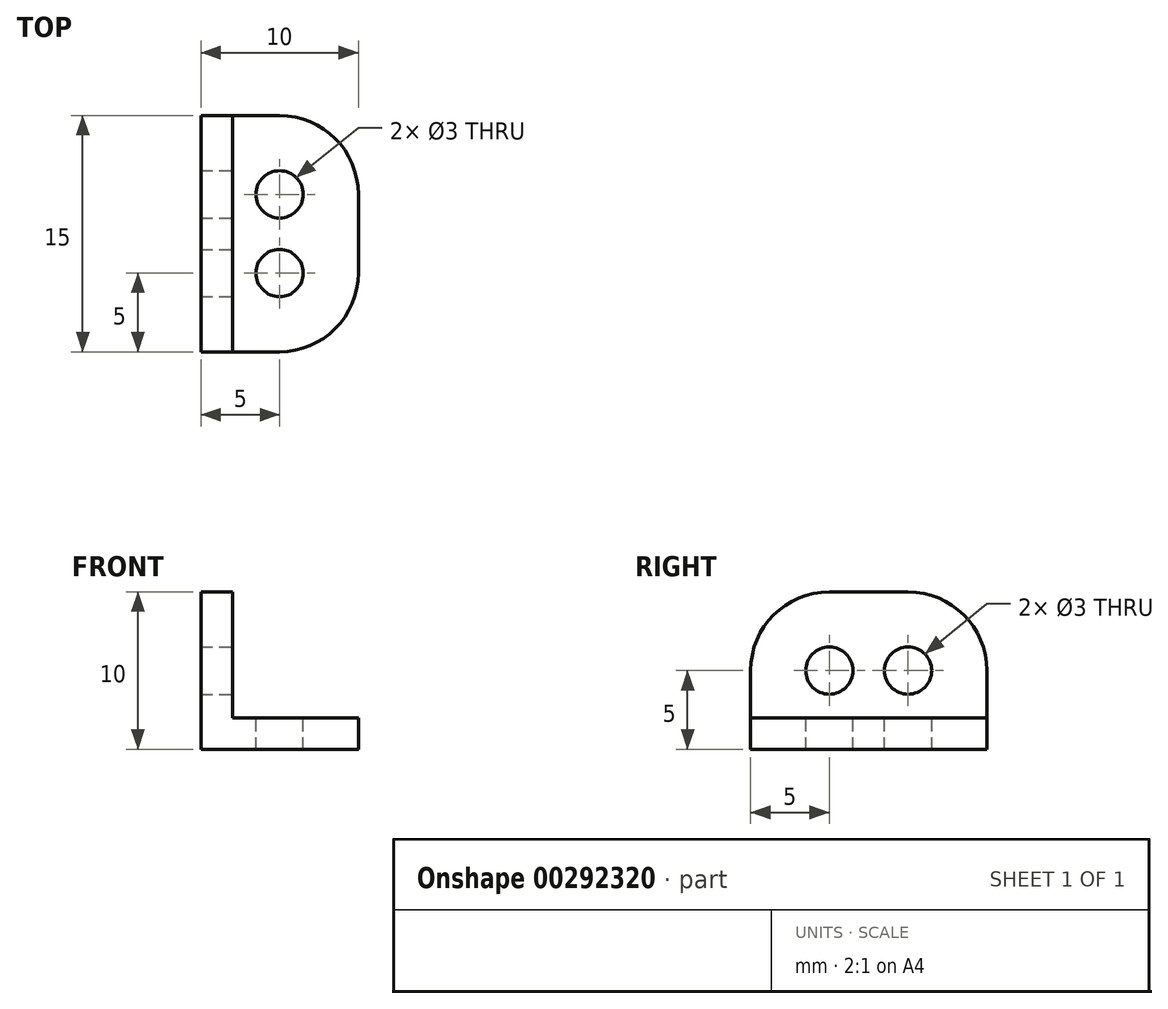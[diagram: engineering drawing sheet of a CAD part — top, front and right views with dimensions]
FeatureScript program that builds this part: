
annotation { "Feature Type Name" : "Feature", "Feature Type Description" : "" }
export const myFeature = defineFeature(function(context is Context, id is Id, definition is map)
    precondition{}
    {
        {
            var Q0;
            Q0=qCreatedBy(makeId("Front.planeOp"),FACE);
            var sketch = newSketch(context, id + "F0", { "sketchPlane" : qUnion([Q0])});
            skLineSegment(sketch, "E0", {"start": v(-5, 5) * mm, "end": v(-5, -5) * mm});
            skLineSegment(sketch, "E1", {"start": v(-5, -5) * mm, "end": v(5, -5) * mm});
            skLineSegment(sketch, "E2", {"start": v(5, -5) * mm, "end": v(5, -3) * mm});
            skLineSegment(sketch, "E3", {"start": v(5, -3) * mm, "end": v(-3, -3) * mm});
            skLineSegment(sketch, "E4", {"start": v(-3, -3) * mm, "end": v(-3, 5) * mm});
            skLineSegment(sketch, "E5", {"start": v(-3, 5) * mm, "end": v(-5, 5) * mm});
            skSolve(sketch);
        }
        {
            var Q0;
            Q0 = qSketchRegion(id + "F0", true);
            extrude(context, id + "F1", {"entities" : qUnion([Q0]), "endBound" : BoundingType.SYMMETRIC, "depth" : 15 * mm});
        }
        {
            var Q0;
            Q0=makeQuery(id+"F1.opExtrude","CAP_EDGE",EDGE,{"disambiguationData":[OSD([sQuery(id+"F0.wireOp",EDGE,"E5")])],"isStart":false});
            var Q1;
            Q1=makeQuery(id+"F1.opExtrude","CAP_EDGE",EDGE,{"disambiguationData":[OSD([sQuery(id+"F0.wireOp",EDGE,"E5")])],"isStart":true});
            var Q2;
            Q2=makeQuery(id+"F1.opExtrude","CAP_EDGE",EDGE,{"disambiguationData":[OSD([sQuery(id+"F0.wireOp",EDGE,"E2")])],"isStart":false});
            var Q3;
            Q3=makeQuery(id+"F1.opExtrude","CAP_EDGE",EDGE,{"disambiguationData":[OSD([sQuery(id+"F0.wireOp",EDGE,"E2")])],"isStart":true});
            fillet(context, id + "F2", {"entities" : qUnion([Q0, Q1, Q2, Q3]), "radius" : 5 * mm, "tangentPropagation" : true, "allowEdgeOverflow" : false});
        }
        {
            var Q0;
            Q0=qCreatedBy(makeId("Right.planeOp"),FACE);
            var sketch = newSketch(context, id + "F3", { "sketchPlane" : qUnion([Q0])});
            skCircle(sketch, "E6", {"center": v(-2.5, 0) * mm, "radius": 1.5 * mm});
            skCircle(sketch, "E7.MirrorC", {"center": v(2.5, 0) * mm, "radius": 1.5 * mm});
            skSolve(sketch);
        }
        {
            var Q0;
            Q0 = qSketchRegion(id + "F3", true);
            extrude(context, id + "F4", {"entities" : qUnion([Q0]), "operationType" : NewBodyOperationType.REMOVE, "oppositeDirection" : true, "depth" : 5 * mm});
        }
        {
            var Q0;
            Q0=qCreatedBy(makeId("Top.planeOp"),FACE);
            var sketch = newSketch(context, id + "F5", { "sketchPlane" : qUnion([Q0])});
            skCircle(sketch, "E8", {"center": v(0, 2.5) * mm, "radius": 1.5 * mm});
            skCircle(sketch, "E9.MirrorC", {"center": v(0, -2.5) * mm, "radius": 1.5 * mm});
            skSolve(sketch);
        }
        {
            var Q0;
            Q0 = qSketchRegion(id + "F5", true);
            extrude(context, id + "F6", {"entities" : qUnion([Q0]), "operationType" : NewBodyOperationType.REMOVE, "oppositeDirection" : true, "depth" : 5 * mm});
        }
    });
